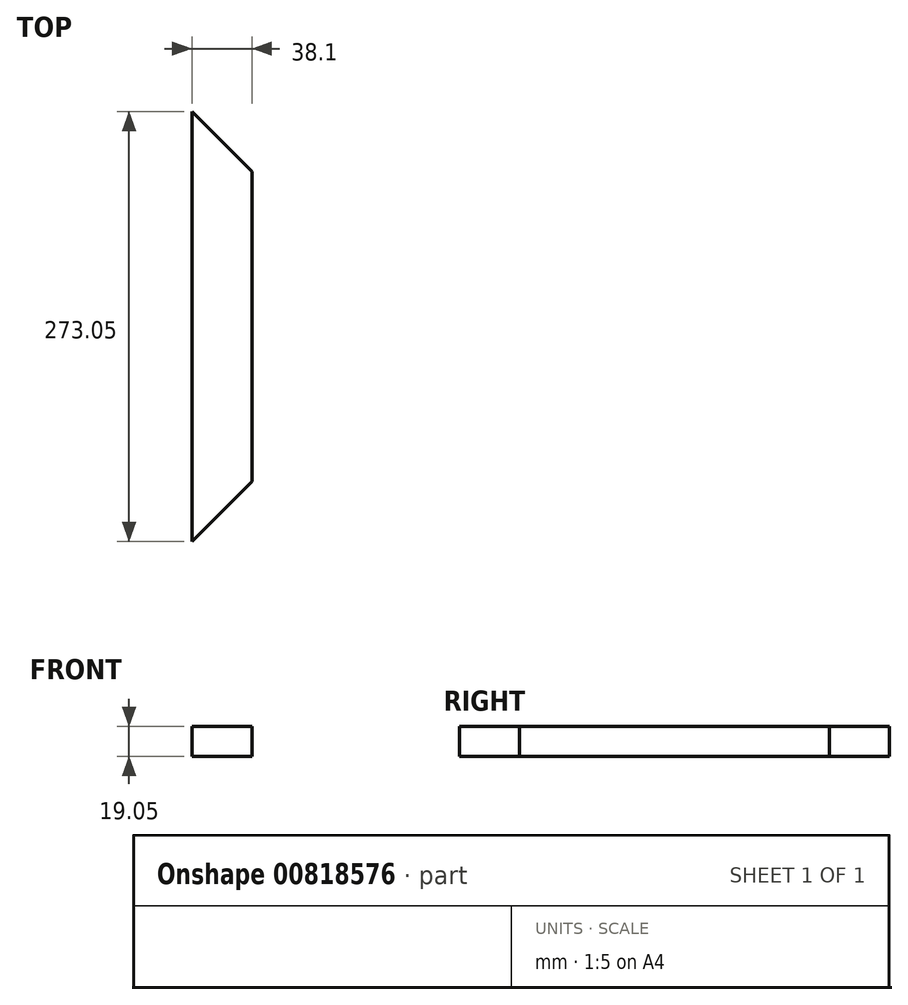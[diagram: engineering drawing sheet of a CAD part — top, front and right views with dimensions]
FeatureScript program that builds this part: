
annotation { "Feature Type Name" : "Feature", "Feature Type Description" : "" }
export const myFeature = defineFeature(function(context is Context, id is Id, definition is map)
    precondition{}
    {
        {
            var Q0;
            Q0=qCreatedBy(makeId("Front.planeOp"),FACE);
            var sketch = newSketch(context, id + "F0", { "sketchPlane" : qUnion([Q0])});
            skLineSegment(sketch, "E0.bottom", {"start": v(-12.82, 8.22) * mm, "end": v(25.28, 8.22) * mm});
            skLineSegment(sketch, "E0.top", {"start": v(-12.82, -10.83) * mm, "end": v(25.28, -10.83) * mm});
            skLineSegment(sketch, "E0.left", {"start": v(-12.82, 8.22) * mm, "end": v(-12.82, -10.83) * mm});
            skLineSegment(sketch, "E0.right", {"start": v(25.28, 8.22) * mm, "end": v(25.28, -10.83) * mm});
            skSolve(sketch);
        }
        {
            var Q0;
            Q0=qSketchRegion(id+"F0",true);
            extrude(context, id + "F1", {"entities" : qUnion([Q0]), "depth" : 273.05 * mm, "offsetDistance" : 25.4 * mm});
        }
        {
            var Q0;
            Q0=makeQuery(id+"F1.opExtrude","SWEPT_FACE",FACE,{"disambiguationData":[OSD([sQuery(id+"F0.wireOp",EDGE,"E0.bottom")])]});
            var sketch = newSketch(context, id + "F2", { "sketchPlane" : qUnion([Q0])});
            skLineSegment(sketch, "E1", {"start": v(-12.82, -273.05) * mm, "end": v(25.28, -234.95) * mm});
            skLineSegment(sketch, "E2", {"start": v(25.28, -234.95) * mm, "end": v(25.28, -273.05) * mm});
            skLineSegment(sketch, "E3", {"start": v(25.28, -273.05) * mm, "end": v(-12.82, -273.05) * mm});
            skLineSegment(sketch, "E4", {"start": v(25.28, 0) * mm, "end": v(25.28, -38.1) * mm});
            skLineSegment(sketch, "E5", {"start": v(25.28, -38.1) * mm, "end": v(-12.82, 0) * mm});
            skLineSegment(sketch, "E6", {"start": v(-12.82, 0) * mm, "end": v(25.28, 0) * mm});
            skSolve(sketch);
        }
        {
            var Q0;
            Q0=qSketchRegion(id+"F2",true);
            extrude(context, id + "F3", {"entities" : qUnion([Q0]), "operationType" : NewBodyOperationType.REMOVE, "oppositeDirection" : true, "depth" : 25.4 * mm, "offsetDistance" : 25.4 * mm});
        }
    });
